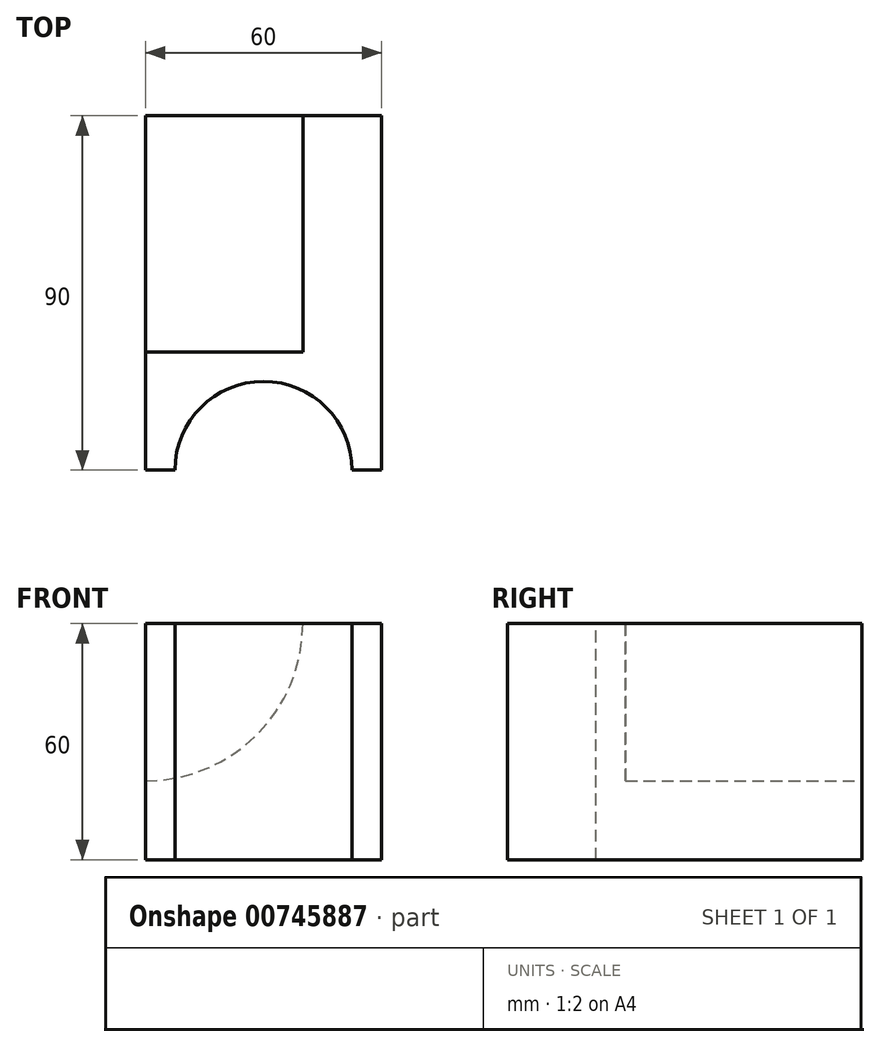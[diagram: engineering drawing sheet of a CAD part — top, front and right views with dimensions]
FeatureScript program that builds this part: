
annotation { "Feature Type Name" : "Feature", "Feature Type Description" : "" }
export const myFeature = defineFeature(function(context is Context, id is Id, definition is map)
    precondition{}
    {
        {
            var Q0;
            Q0=qCreatedBy(makeId("Front.planeOp"),FACE);
            var sketch = newSketch(context, id + "F0", { "sketchPlane" : qUnion([Q0])});
            skLineSegment(sketch, "E0.bottom", {"start": v(0, 0) * mm, "end": v(60, 0) * mm});
            skLineSegment(sketch, "E0.top", {"start": v(0, 60) * mm, "end": v(60, 60) * mm});
            skLineSegment(sketch, "E0.left", {"start": v(0, 0) * mm, "end": v(0, 60) * mm});
            skLineSegment(sketch, "E0.right", {"start": v(60, 0) * mm, "end": v(60, 60) * mm});
            skSolve(sketch);
        }
        {
            var Q0;
            Q0 = qSketchRegion(id + "F0", true);
            extrude(context, id + "F1", {"entities" : qUnion([Q0]), "depth" : 90 * mm, "offsetDistance" : 25 * mm});
        }
        {
            var Q0;
            Q0=makeQuery(id+"F1.opExtrude","SWEPT_FACE",FACE,{"disambiguationData":[OSD([sQuery(id+"F0.wireOp",EDGE,"E0.top")])]});
            var sketch = newSketch(context, id + "F2", { "sketchPlane" : qUnion([Q0])});
            skArc(sketch, "E1", {"start": v(52.5, -90) * mm, "mid": v(30, -67.5) * mm, "end": v(7.5, -90) * mm});
            skSolve(sketch);
        }
        {
            var Q0;
            Q0 = qSketchRegion(id + "F2", true);
            var Q1;
            {var subQ0=sQuery(id+"F2.wireOp",EDGE,"E1");Q1=makeQuery(id+"F2.imprint","IMPRINT",FACE,{"disambiguationData":[TD([[makeQuery(id+"F2.imprint","IMPRINT",EDGE,{"derivedFrom":subQ0}),1.0]])]});}
            extrude(context, id + "F3", {"entities" : qUnion([Q0, Q1]), "operationType" : NewBodyOperationType.REMOVE, "oppositeDirection" : true, "depth" : 74.5 * mm, "offsetDistance" : 25 * mm});
        }
        {
            var Q0;
            Q0=makeQuery(id+"F1.opExtrude","CAP_FACE",FACE,{"disambiguationData":[OSD([sQuery(id+"F0.wireOp",EDGE,"E0.bottom"),sQuery(id+"F0.wireOp",EDGE,"E0.top"),sQuery(id+"F0.wireOp",EDGE,"E0.left"),sQuery(id+"F0.wireOp",EDGE,"E0.right")])],"isStart":true});
            var sketch = newSketch(context, id + "F4", { "sketchPlane" : qUnion([Q0])});
            skArc(sketch, "E2", {"start": v(-40, 60) * mm, "mid": v(-28.28, 31.72) * mm, "end": v(0, 20) * mm});
            skSolve(sketch);
        }
        {
            var Q0;
            Q0 = qSketchRegion(id + "F4", true);
            var Q1;
            {var subQ0=sQuery(id+"F4.wireOp",EDGE,"E2");Q1=makeQuery(id+"F4.imprint","IMPRINT",FACE,{"disambiguationData":[TD([[makeQuery(id+"F4.imprint","IMPRINT",EDGE,{"derivedFrom":subQ0}),1.0]])]});}
            extrude(context, id + "F5", {"entities" : qUnion([Q0, Q1]), "operationType" : NewBodyOperationType.REMOVE, "oppositeDirection" : true, "depth" : 60 * mm, "offsetDistance" : 25 * mm});
        }
    });
